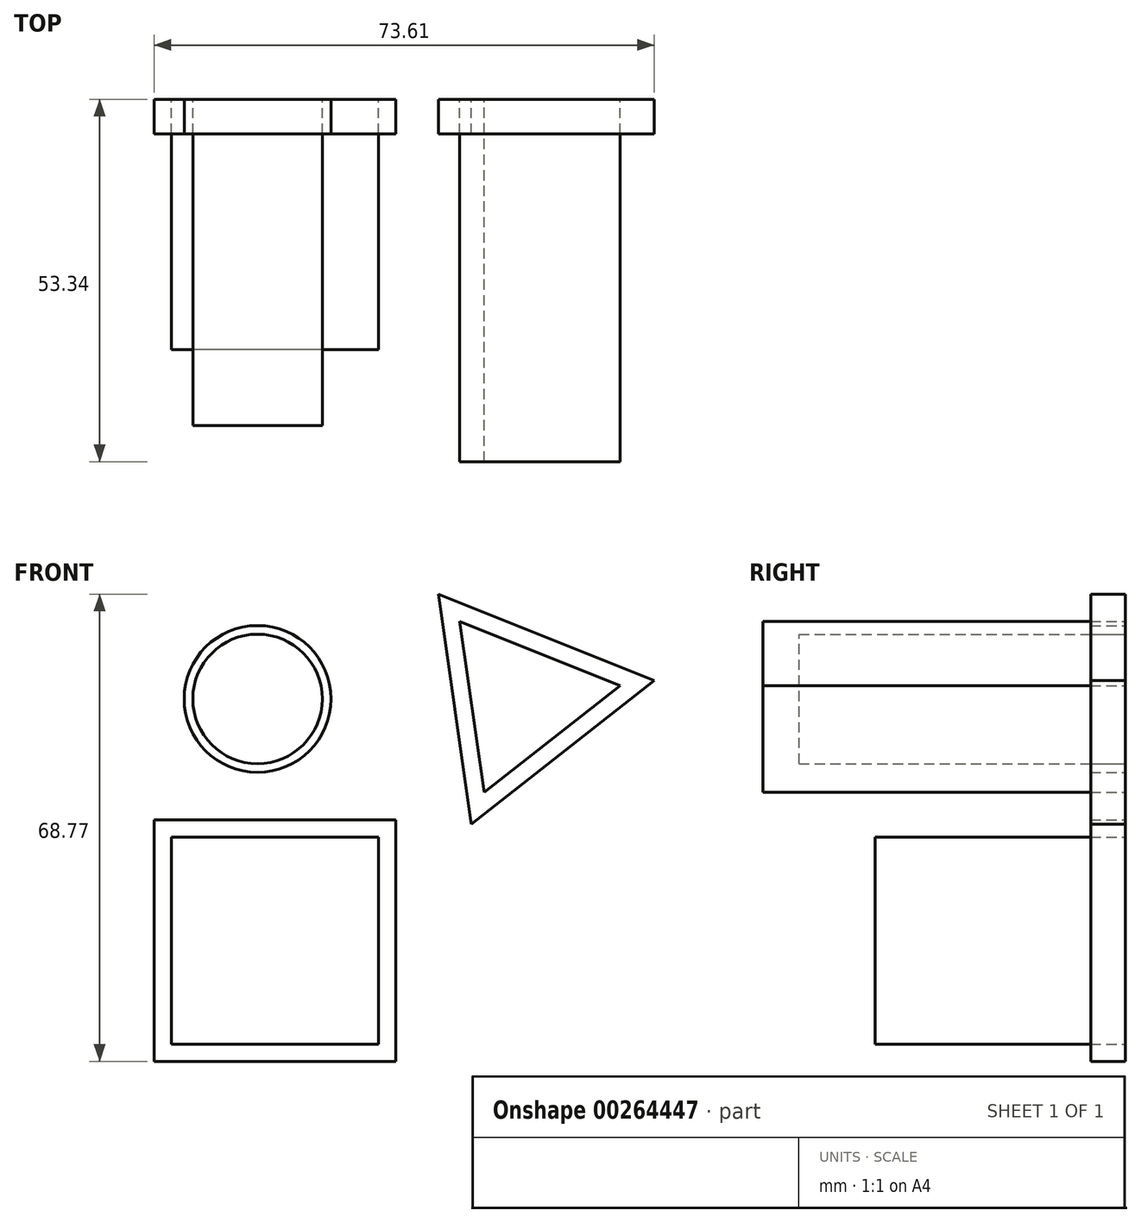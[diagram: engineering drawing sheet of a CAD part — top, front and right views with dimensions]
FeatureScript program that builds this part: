
annotation { "Feature Type Name" : "Feature", "Feature Type Description" : "" }
export const myFeature = defineFeature(function(context is Context, id is Id, definition is map)
    precondition{}
    {
        {
            var Q0;
            Q0=qCreatedBy(makeId("Front.planeOp"),FACE);
            var sketch = newSketch(context, id + "F0", { "sketchPlane" : qUnion([Q0])});
            skLineSegment(sketch, "E0.bottom", {"start": v(38.1, 38.1) * mm, "end": v(-38.1, 38.1) * mm, "construction": true});
            skLineSegment(sketch, "E0.top", {"start": v(38.1, -38.1) * mm, "end": v(-38.1, -38.1) * mm, "construction": true});
            skLineSegment(sketch, "E0.left", {"start": v(38.1, 38.1) * mm, "end": v(38.1, -38.1) * mm, "construction": true});
            skLineSegment(sketch, "E0.right", {"start": v(-38.1, 38.1) * mm, "end": v(-38.1, -38.1) * mm, "construction": true});
            skPoint(sketch, "E0.middle", {"position": v(0, 0) * mm});
            skCircle(sketch, "E1", {"center": v(-17.78, 17.78) * mm, "radius": 9.53 * mm});
            skLineSegment(sketch, "E2", {"start": v(-17.78, 17.78) * mm, "end": v(-17.78, 38.1) * mm, "construction": true});
            skLineSegment(sketch, "E3", {"start": v(-17.78, 17.78) * mm, "end": v(-38.1, 17.78) * mm, "construction": true});
            skLineSegment(sketch, "E4", {"start": v(11.99, 29.21) * mm, "end": v(35.56, 19.75) * mm});
            skLineSegment(sketch, "E5", {"start": v(35.56, 19.75) * mm, "end": v(15.58, 4.07) * mm});
            skLineSegment(sketch, "E6", {"start": v(11.99, 29.21) * mm, "end": v(15.58, 4.07) * mm});
            skLineSegment(sketch, "E7.bottom", {"start": v(0, -2.54) * mm, "end": v(-30.48, -2.54) * mm});
            skLineSegment(sketch, "E7.top", {"start": v(0, -33.02) * mm, "end": v(-30.48, -33.02) * mm});
            skLineSegment(sketch, "E7.left", {"start": v(0, -2.54) * mm, "end": v(0, -33.02) * mm});
            skLineSegment(sketch, "E7.right", {"start": v(-30.48, -2.54) * mm, "end": v(-30.48, -33.02) * mm});
            skPoint(sketch, "E7.middle", {"position": v(-15.24, -17.78) * mm});
            skCircle(sketch, "E8", {"center": v(-17.78, 17.78) * mm, "radius": 10.8 * mm});
            skLineSegment(sketch, "E9.bottom", {"start": v(2.54, 0) * mm, "end": v(-33.02, 0) * mm});
            skLineSegment(sketch, "E9.top", {"start": v(2.54, -35.56) * mm, "end": v(-33.02, -35.56) * mm});
            skLineSegment(sketch, "E9.left", {"start": v(2.54, 0) * mm, "end": v(2.54, -35.56) * mm});
            skLineSegment(sketch, "E9.right", {"start": v(-33.02, 0) * mm, "end": v(-33.02, -35.56) * mm});
            skLineSegment(sketch, "E10", {"start": v(8.85, 33.2) * mm, "end": v(13.69, -0.65) * mm});
            skPoint(sketch, "E10.endSnap0", {"position": v(-15.24, -2.54) * mm});
            skLineSegment(sketch, "E11", {"start": v(13.69, -0.65) * mm, "end": v(40.59, 20.47) * mm});
            skLineSegment(sketch, "E12", {"start": v(40.59, 20.47) * mm, "end": v(8.47, 33.36) * mm});
            skPoint(sketch, "E13.orphan", {"position": v(9.42, 29.21) * mm});
            skSolve(sketch);
        }
        {
            var Q0;
            Q0=makeQuery(id+"F0.imprint","IMPRINT",FACE,{"disambiguationData":[TD([[makeQuery(id+"F0.imprint","IMPRINT",EDGE,{"derivedFrom":sQuery(id+"F0.wireOp",EDGE,"E1")}),1.0]])]});
            extrude(context, id + "F1", {"entities" : qUnion([Q0]), "depth" : 48 * mm});
        }
        {
            var Q0;
            Q0=makeQuery(id+"F0.imprint","IMPRINT",FACE,{"disambiguationData":[TD([[makeQuery(id+"F0.imprint","IMPRINT",EDGE,{"derivedFrom":sQuery(id+"F0.wireOp",EDGE,"E7.bottom")}),1.0]])]});
            extrude(context, id + "F2", {"entities" : qUnion([Q0]), "depth" : 36.83 * mm});
        }
        {
            var Q0;
            Q0=makeQuery(id+"F0.imprint","IMPRINT",FACE,{"disambiguationData":[TD([[makeQuery(id+"F0.imprint","IMPRINT",EDGE,{"derivedFrom":sQuery(id+"F0.wireOp",EDGE,"E4")}),-1.0]])]});
            extrude(context, id + "F3", {"entities" : qUnion([Q0]), "depth" : 53.34 * mm});
        }
        {
            var Q0;
            Q0=makeQuery(id+"F0.imprint","IMPRINT",FACE,{"disambiguationData":[TD([[makeQuery(id+"F0.imprint","IMPRINT",EDGE,{"derivedFrom":sQuery(id+"F0.wireOp",EDGE,"E1")}),-1.0]])]});
            var Q1;
            Q1=makeQuery(id+"F0.imprint","IMPRINT",FACE,{"disambiguationData":[TD([[makeQuery(id+"F0.imprint","IMPRINT",EDGE,{"derivedFrom":sQuery(id+"F0.wireOp",EDGE,"E7.bottom")}),-1.0]])]});
            var Q2;
            Q2=makeQuery(id+"F0.imprint","IMPRINT",FACE,{"disambiguationData":[TD([[makeQuery(id+"F0.imprint","IMPRINT",EDGE,{"derivedFrom":sQuery(id+"F0.wireOp",EDGE,"E4")}),1.0]])]});
            extrude(context, id + "F4", {"entities" : qUnion([Q0, Q1, Q2]), "depth" : 5.08 * mm});
        }
        {
            var Q0;
            Q0=qCreatedBy(makeId("Front.planeOp"),FACE);
            var sketch = newSketch(context, id + "F5", { "sketchPlane" : qUnion([Q0])});
            skCircle(sketch, "E14", {"center": v(-17.78, 17.78) * mm, "radius": 10.76 * mm});
            skLineSegment(sketch, "E15.bottom", {"start": v(2.55, 0) * mm, "end": v(-33.14, 0) * mm});
            skLineSegment(sketch, "E15.top", {"start": v(2.55, -35.64) * mm, "end": v(-33.14, -35.64) * mm});
            skLineSegment(sketch, "E15.left", {"start": v(2.55, 0) * mm, "end": v(2.55, -35.64) * mm});
            skLineSegment(sketch, "E15.right", {"start": v(-33.14, 0) * mm, "end": v(-33.14, -35.64) * mm});
            skPoint(sketch, "E15.middle", {"position": v(-15.3, -17.82) * mm});
            skLineSegment(sketch, "E16", {"start": v(8.85, 33.2) * mm, "end": v(40.59, 20.47) * mm});
            skLineSegment(sketch, "E17", {"start": v(40.59, 20.47) * mm, "end": v(13.69, -0.65) * mm});
            skLineSegment(sketch, "E18", {"start": v(13.69, -0.65) * mm, "end": v(8.85, 33.2) * mm});
            skSolve(sketch);
        }
        {
            var Q0;
            Q0=sQuery(id+"F5.wireOp",EDGE,"E14");
            extrude(context, id + "F6", {"bodyType" : ToolBodyType.SURFACE, "surfaceEntities" : qUnion([Q0]), "depth" : 2.54 * mm});
        }
        {
            var Q0;
            Q0=sQuery(id+"F0.wireOp",EDGE,"E9.bottom");
            var Q1;
            Q1=sQuery(id+"F0.wireOp",EDGE,"E9.right");
            var Q2;
            Q2=sQuery(id+"F0.wireOp",EDGE,"E9.top");
            var Q3;
            Q3=sQuery(id+"F0.wireOp",EDGE,"E9.left");
            extrude(context, id + "F7", {"bodyType" : ToolBodyType.SURFACE, "surfaceEntities" : qUnion([Q0, Q1, Q2, Q3]), "depth" : 2.54 * mm});
        }
        {
            var Q0;
            Q0=sQuery(id+"F5.wireOp",EDGE,"E16");
            var Q1;
            Q1=sQuery(id+"F5.wireOp",EDGE,"E18");
            var Q2;
            Q2=sQuery(id+"F5.wireOp",EDGE,"E17");
            extrude(context, id + "F8", {"bodyType" : ToolBodyType.SURFACE, "surfaceEntities" : qUnion([Q0, Q1, Q2]), "depth" : 2.54 * mm});
        }
    });
